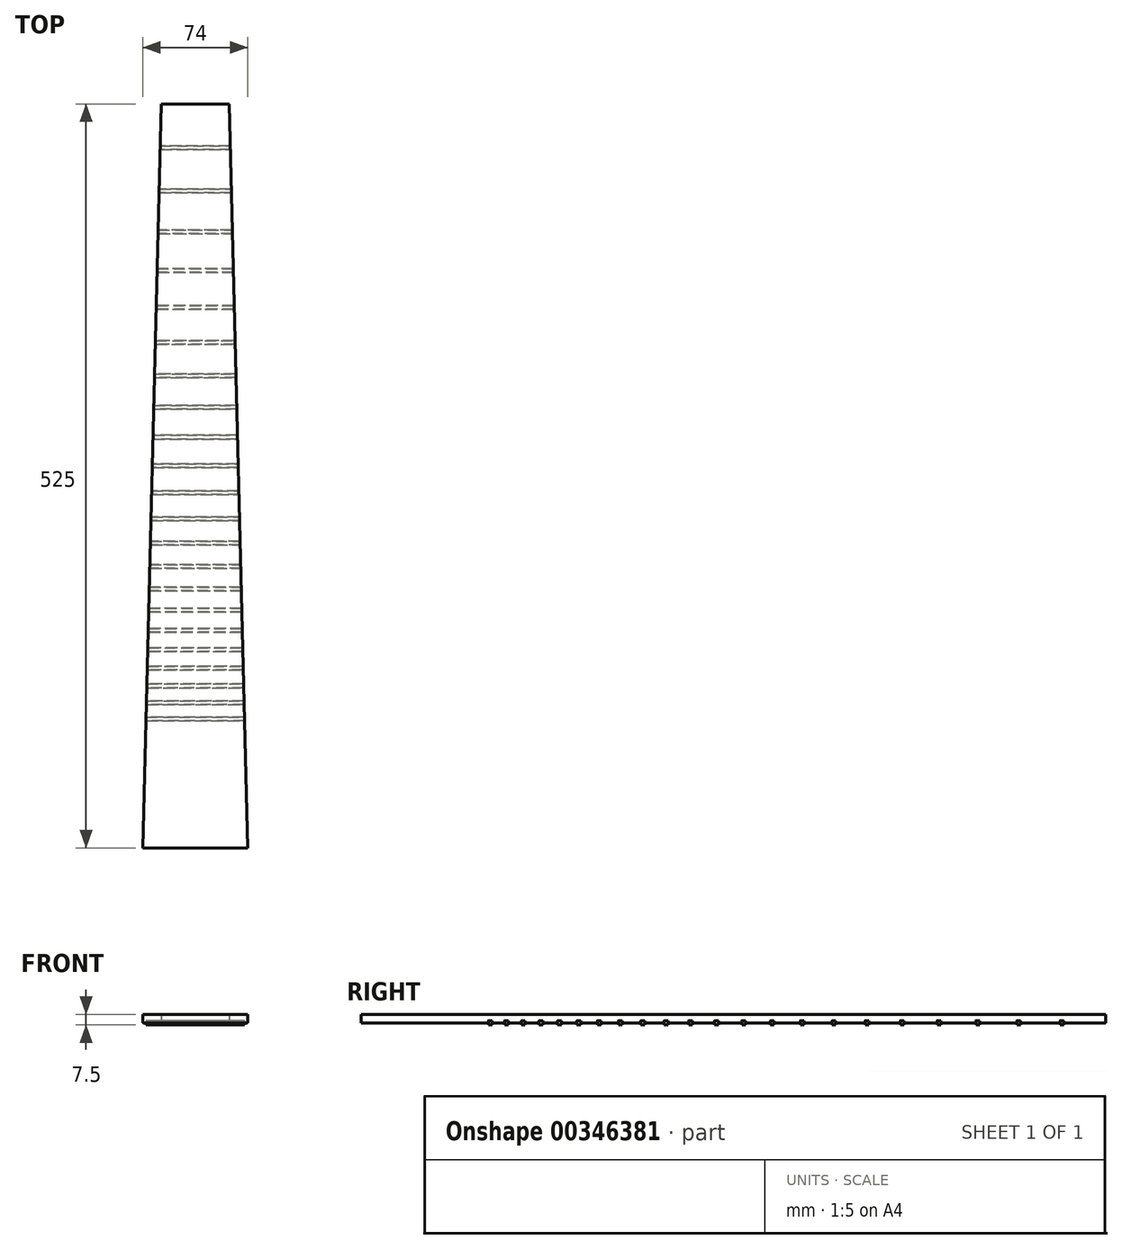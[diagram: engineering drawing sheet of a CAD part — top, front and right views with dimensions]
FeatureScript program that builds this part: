
annotation { "Feature Type Name" : "Feature", "Feature Type Description" : "" }
export const myFeature = defineFeature(function(context is Context, id is Id, definition is map)
    precondition{}
    {
        {
            var Q0;
            Q0=qCreatedBy(makeId("Top.planeOp"),FACE);
            var sketch = newSketch(context, id + "F0", { "sketchPlane" : qUnion([Q0])});
            skLineSegment(sketch, "E0", {"start": v(0, 0) * mm, "end": v(0, 525) * mm, "construction": true});
            skLineSegment(sketch, "E1", {"start": v(0, 525) * mm, "end": v(-24, 525) * mm});
            skLineSegment(sketch, "E2", {"start": v(0, 0) * mm, "end": v(-37, 0) * mm});
            skLineSegment(sketch, "E3", {"start": v(-37, 0) * mm, "end": v(-24, 525) * mm});
            skLineSegment(sketch, "E4", {"start": v(-24.73, 495.53) * mm, "end": v(0, 495.53) * mm});
            skLineSegment(sketch, "E5", {"start": v(-24.8, 492.92) * mm, "end": v(0, 492.92) * mm});
            skLineSegment(sketch, "E6", {"start": v(-25.48, 465.1) * mm, "end": v(0, 465.1) * mm});
            skLineSegment(sketch, "E7", {"start": v(-25.55, 462.49) * mm, "end": v(0, 462.49) * mm});
            skLineSegment(sketch, "E8", {"start": v(-26.2, 436.24) * mm, "end": v(0, 436.24) * mm});
            skLineSegment(sketch, "E9", {"start": v(-26.26, 433.62) * mm, "end": v(0, 433.62) * mm});
            skLineSegment(sketch, "E10", {"start": v(-26.88, 408.84) * mm, "end": v(0, 408.84) * mm});
            skLineSegment(sketch, "E11", {"start": v(-26.94, 406.23) * mm, "end": v(0, 406.23) * mm});
            skLineSegment(sketch, "E12", {"start": v(-27.52, 382.84) * mm, "end": v(0, 382.84) * mm});
            skLineSegment(sketch, "E13", {"start": v(-27.58, 380.22) * mm, "end": v(0, 380.22) * mm});
            skLineSegment(sketch, "E14", {"start": v(-28.13, 358.15) * mm, "end": v(0, 358.15) * mm});
            skLineSegment(sketch, "E15", {"start": v(-28.2, 355.53) * mm, "end": v(0, 355.53) * mm});
            skLineSegment(sketch, "E16", {"start": v(-28.71, 334.7) * mm, "end": v(0, 334.7) * mm});
            skLineSegment(sketch, "E17", {"start": v(-28.78, 332.08) * mm, "end": v(0, 332.08) * mm});
            skLineSegment(sketch, "E18", {"start": v(-29.26, 312.42) * mm, "end": v(0, 312.42) * mm});
            skLineSegment(sketch, "E19", {"start": v(-29.33, 309.8) * mm, "end": v(0, 309.8) * mm});
            skLineSegment(sketch, "E20", {"start": v(-29.79, 291.24) * mm, "end": v(0, 291.24) * mm});
            skLineSegment(sketch, "E21", {"start": v(-29.85, 288.62) * mm, "end": v(0, 288.62) * mm});
            skLineSegment(sketch, "E22", {"start": v(-30.29, 271.1) * mm, "end": v(0, 271.1) * mm});
            skLineSegment(sketch, "E23", {"start": v(-30.35, 268.48) * mm, "end": v(0, 268.48) * mm});
            skLineSegment(sketch, "E24", {"start": v(-30.76, 251.95) * mm, "end": v(0, 251.95) * mm});
            skLineSegment(sketch, "E25", {"start": v(-30.83, 249.33) * mm, "end": v(0, 249.33) * mm});
            skLineSegment(sketch, "E26", {"start": v(-31.21, 233.72) * mm, "end": v(0, 233.72) * mm});
            skLineSegment(sketch, "E27", {"start": v(-31.28, 231.1) * mm, "end": v(0, 231.1) * mm});
            skLineSegment(sketch, "E28", {"start": v(-31.64, 216.37) * mm, "end": v(0, 216.37) * mm});
            skLineSegment(sketch, "E29", {"start": v(-31.7, 213.76) * mm, "end": v(0, 213.76) * mm});
            skLineSegment(sketch, "E30", {"start": v(-32.05, 199.85) * mm, "end": v(0, 199.85) * mm});
            skLineSegment(sketch, "E31", {"start": v(-32.12, 197.23) * mm, "end": v(0, 197.23) * mm});
            skLineSegment(sketch, "E32", {"start": v(-32.44, 184.1) * mm, "end": v(0, 184.1) * mm});
            skLineSegment(sketch, "E33", {"start": v(-32.5, 181.5) * mm, "end": v(0, 181.5) * mm});
            skLineSegment(sketch, "E34", {"start": v(-32.81, 169.1) * mm, "end": v(0, 169.1) * mm});
            skLineSegment(sketch, "E35", {"start": v(-32.88, 166.49) * mm, "end": v(0, 166.49) * mm});
            skLineSegment(sketch, "E36", {"start": v(-33.17, 154.8) * mm, "end": v(0, 154.8) * mm});
            skLineSegment(sketch, "E37", {"start": v(-33.23, 152.18) * mm, "end": v(0, 152.18) * mm});
            skLineSegment(sketch, "E38", {"start": v(-33.5, 141.14) * mm, "end": v(0, 141.14) * mm});
            skLineSegment(sketch, "E39", {"start": v(-33.57, 138.53) * mm, "end": v(0, 138.53) * mm});
            skLineSegment(sketch, "E40", {"start": v(-33.83, 128.1) * mm, "end": v(0, 128.1) * mm});
            skLineSegment(sketch, "E41", {"start": v(-33.9, 125.5) * mm, "end": v(0, 125.5) * mm});
            skLineSegment(sketch, "E42", {"start": v(-34.14, 115.66) * mm, "end": v(0, 115.66) * mm});
            skLineSegment(sketch, "E43", {"start": v(-34.2, 113.04) * mm, "end": v(0, 113.04) * mm});
            skLineSegment(sketch, "E44", {"start": v(-34.43, 103.76) * mm, "end": v(0, 103.76) * mm});
            skLineSegment(sketch, "E45", {"start": v(-34.5, 101.14) * mm, "end": v(0, 101.14) * mm});
            skLineSegment(sketch, "E46", {"start": v(-34.71, 92.38) * mm, "end": v(0, 92.38) * mm});
            skLineSegment(sketch, "E47", {"start": v(-34.78, 89.77) * mm, "end": v(0, 89.77) * mm});
            skLineSegment(sketch, "E48.MirrorCS", {"start": v(0, 525) * mm, "end": v(24, 525) * mm});
            skLineSegment(sketch, "E49.MirrorCS", {"start": v(37, 0) * mm, "end": v(24, 525) * mm});
            skLineSegment(sketch, "E50.MirrorCS", {"start": v(24.73, 495.53) * mm, "end": v(0, 495.53) * mm});
            skLineSegment(sketch, "E51.MirrorCS", {"start": v(24.8, 492.92) * mm, "end": v(0, 492.92) * mm});
            skLineSegment(sketch, "E52.MirrorCS", {"start": v(25.48, 465.1) * mm, "end": v(0, 465.1) * mm});
            skLineSegment(sketch, "E53.MirrorCS", {"start": v(25.55, 462.49) * mm, "end": v(0, 462.49) * mm});
            skLineSegment(sketch, "E54.MirrorCS", {"start": v(26.2, 436.24) * mm, "end": v(0, 436.24) * mm});
            skLineSegment(sketch, "E55.MirrorCS", {"start": v(26.26, 433.62) * mm, "end": v(0, 433.62) * mm});
            skLineSegment(sketch, "E56.MirrorCS", {"start": v(26.88, 408.84) * mm, "end": v(0, 408.84) * mm});
            skLineSegment(sketch, "E57.MirrorCS", {"start": v(26.94, 406.23) * mm, "end": v(0, 406.23) * mm});
            skLineSegment(sketch, "E58.MirrorCS", {"start": v(27.52, 382.84) * mm, "end": v(0, 382.84) * mm});
            skLineSegment(sketch, "E59.MirrorCS", {"start": v(27.58, 380.22) * mm, "end": v(0, 380.22) * mm});
            skLineSegment(sketch, "E60.MirrorCS", {"start": v(28.13, 358.15) * mm, "end": v(0, 358.15) * mm});
            skLineSegment(sketch, "E61.MirrorCS", {"start": v(28.2, 355.53) * mm, "end": v(0, 355.53) * mm});
            skLineSegment(sketch, "E62.MirrorCS", {"start": v(28.71, 334.7) * mm, "end": v(0, 334.7) * mm});
            skLineSegment(sketch, "E63.MirrorCS", {"start": v(28.78, 332.08) * mm, "end": v(0, 332.08) * mm});
            skLineSegment(sketch, "E64.MirrorCS", {"start": v(29.26, 312.42) * mm, "end": v(0, 312.42) * mm});
            skLineSegment(sketch, "E65.MirrorCS", {"start": v(29.33, 309.8) * mm, "end": v(0, 309.8) * mm});
            skLineSegment(sketch, "E66.MirrorCS", {"start": v(29.79, 291.24) * mm, "end": v(0, 291.24) * mm});
            skLineSegment(sketch, "E67.MirrorCS", {"start": v(29.85, 288.62) * mm, "end": v(0, 288.62) * mm});
            skLineSegment(sketch, "E68.MirrorCS", {"start": v(30.29, 271.1) * mm, "end": v(0, 271.1) * mm});
            skLineSegment(sketch, "E69.MirrorCS", {"start": v(30.35, 268.48) * mm, "end": v(0, 268.48) * mm});
            skLineSegment(sketch, "E70.MirrorCS", {"start": v(30.76, 251.95) * mm, "end": v(0, 251.95) * mm});
            skLineSegment(sketch, "E71.MirrorCS", {"start": v(30.83, 249.33) * mm, "end": v(0, 249.33) * mm});
            skLineSegment(sketch, "E72.MirrorCS", {"start": v(31.21, 233.72) * mm, "end": v(0, 233.72) * mm});
            skLineSegment(sketch, "E73.MirrorCS", {"start": v(31.28, 231.1) * mm, "end": v(0, 231.1) * mm});
            skLineSegment(sketch, "E74.MirrorCS", {"start": v(31.64, 216.37) * mm, "end": v(0, 216.37) * mm});
            skLineSegment(sketch, "E75.MirrorCS", {"start": v(31.7, 213.76) * mm, "end": v(0, 213.76) * mm});
            skLineSegment(sketch, "E76.MirrorCS", {"start": v(32.05, 199.85) * mm, "end": v(0, 199.85) * mm});
            skLineSegment(sketch, "E77.MirrorCS", {"start": v(32.12, 197.23) * mm, "end": v(0, 197.23) * mm});
            skLineSegment(sketch, "E78.MirrorCS", {"start": v(32.44, 184.1) * mm, "end": v(0, 184.1) * mm});
            skLineSegment(sketch, "E79.MirrorCS", {"start": v(32.5, 181.5) * mm, "end": v(0, 181.5) * mm});
            skLineSegment(sketch, "E80.MirrorCS", {"start": v(32.81, 169.1) * mm, "end": v(0, 169.1) * mm});
            skLineSegment(sketch, "E81.MirrorCS", {"start": v(32.88, 166.49) * mm, "end": v(0, 166.49) * mm});
            skLineSegment(sketch, "E82.MirrorCS", {"start": v(33.17, 154.8) * mm, "end": v(0, 154.8) * mm});
            skLineSegment(sketch, "E83.MirrorCS", {"start": v(33.23, 152.18) * mm, "end": v(0, 152.18) * mm});
            skLineSegment(sketch, "E84.MirrorCS", {"start": v(33.5, 141.14) * mm, "end": v(0, 141.14) * mm});
            skLineSegment(sketch, "E85.MirrorCS", {"start": v(33.57, 138.53) * mm, "end": v(0, 138.53) * mm});
            skLineSegment(sketch, "E86.MirrorCS", {"start": v(33.83, 128.1) * mm, "end": v(0, 128.1) * mm});
            skLineSegment(sketch, "E87.MirrorCS", {"start": v(33.9, 125.5) * mm, "end": v(0, 125.5) * mm});
            skLineSegment(sketch, "E88.MirrorCS", {"start": v(34.14, 115.66) * mm, "end": v(0, 115.66) * mm});
            skLineSegment(sketch, "E89.MirrorCS", {"start": v(34.2, 113.04) * mm, "end": v(0, 113.04) * mm});
            skLineSegment(sketch, "E90.MirrorCS", {"start": v(34.43, 103.76) * mm, "end": v(0, 103.76) * mm});
            skLineSegment(sketch, "E91.MirrorCS", {"start": v(34.5, 101.14) * mm, "end": v(0, 101.14) * mm});
            skLineSegment(sketch, "E92.MirrorCS", {"start": v(0, 0) * mm, "end": v(37, 0) * mm});
            skLineSegment(sketch, "E93.MirrorCS", {"start": v(34.71, 92.38) * mm, "end": v(0, 92.38) * mm});
            skLineSegment(sketch, "E94.MirrorCS", {"start": v(34.78, 89.77) * mm, "end": v(0, 89.77) * mm});
            skSolve(sketch);
        }
        {
            var Q0;
            Q0=qSketchRegion(id+"F0",true);
            extrude(context, id + "F1", {"entities" : qUnion([Q0]), "depth" : 6 * mm});
        }
        {
            var Q0;
            {var subQ1=sQuery(id+"F0.wireOp",EDGE,"E4");Q0=makeQuery(id+"F0.imprint","IMPRINT",FACE,{"disambiguationData":[TD([[makeQuery(id+"F0.imprint","IMPRINT",EDGE,{"derivedFrom":subQ1}),-1.0]])]});}
            var Q1;
            {var subQ1=sQuery(id+"F0.wireOp",EDGE,"E6");Q1=makeQuery(id+"F0.imprint","IMPRINT",FACE,{"disambiguationData":[TD([[makeQuery(id+"F0.imprint","IMPRINT",EDGE,{"derivedFrom":subQ1}),-1.0]])]});}
            var Q2;
            {var subQ1=sQuery(id+"F0.wireOp",EDGE,"E8");Q2=makeQuery(id+"F0.imprint","IMPRINT",FACE,{"disambiguationData":[TD([[makeQuery(id+"F0.imprint","IMPRINT",EDGE,{"derivedFrom":subQ1}),-1.0]])]});}
            var Q3;
            {var subQ0=sQuery(id+"F0.wireOp",EDGE,"E10");Q3=makeQuery(id+"F0.imprint","IMPRINT",FACE,{"disambiguationData":[TD([[makeQuery(id+"F0.imprint","IMPRINT",EDGE,{"derivedFrom":subQ0}),-1.0]])]});}
            var Q4;
            {var subQ1=sQuery(id+"F0.wireOp",EDGE,"E12");Q4=makeQuery(id+"F0.imprint","IMPRINT",FACE,{"disambiguationData":[TD([[makeQuery(id+"F0.imprint","IMPRINT",EDGE,{"derivedFrom":subQ1}),-1.0]])]});}
            var Q5;
            {var subQ1=sQuery(id+"F0.wireOp",EDGE,"E14");Q5=makeQuery(id+"F0.imprint","IMPRINT",FACE,{"disambiguationData":[TD([[makeQuery(id+"F0.imprint","IMPRINT",EDGE,{"derivedFrom":subQ1}),-1.0]])]});}
            var Q6;
            {var subQ1=sQuery(id+"F0.wireOp",EDGE,"E16");Q6=makeQuery(id+"F0.imprint","IMPRINT",FACE,{"disambiguationData":[TD([[makeQuery(id+"F0.imprint","IMPRINT",EDGE,{"derivedFrom":subQ1}),-1.0]])]});}
            var Q7;
            {var subQ4=sQuery(id+"F0.wireOp",EDGE,"E18");Q7=makeQuery(id+"F0.imprint","IMPRINT",FACE,{"disambiguationData":[TD([[makeQuery(id+"F0.imprint","IMPRINT",EDGE,{"derivedFrom":subQ4}),-1.0]])]});}
            var Q8;
            {var subQ0=sQuery(id+"F0.wireOp",EDGE,"E20");Q8=makeQuery(id+"F0.imprint","IMPRINT",FACE,{"disambiguationData":[TD([[makeQuery(id+"F0.imprint","IMPRINT",EDGE,{"derivedFrom":subQ0}),-1.0]])]});}
            var Q9;
            {var subQ1=sQuery(id+"F0.wireOp",EDGE,"E22");Q9=makeQuery(id+"F0.imprint","IMPRINT",FACE,{"disambiguationData":[TD([[makeQuery(id+"F0.imprint","IMPRINT",EDGE,{"derivedFrom":subQ1}),-1.0]])]});}
            var Q10;
            {var subQ1=sQuery(id+"F0.wireOp",EDGE,"E24");Q10=makeQuery(id+"F0.imprint","IMPRINT",FACE,{"disambiguationData":[TD([[makeQuery(id+"F0.imprint","IMPRINT",EDGE,{"derivedFrom":subQ1}),-1.0]])]});}
            var Q11;
            {var subQ1=sQuery(id+"F0.wireOp",EDGE,"E26");Q11=makeQuery(id+"F0.imprint","IMPRINT",FACE,{"disambiguationData":[TD([[makeQuery(id+"F0.imprint","IMPRINT",EDGE,{"derivedFrom":subQ1}),-1.0]])]});}
            var Q12;
            {var subQ4=sQuery(id+"F0.wireOp",EDGE,"E28");Q12=makeQuery(id+"F0.imprint","IMPRINT",FACE,{"disambiguationData":[TD([[makeQuery(id+"F0.imprint","IMPRINT",EDGE,{"derivedFrom":subQ4}),-1.0]])]});}
            var Q13;
            {var subQ0=sQuery(id+"F0.wireOp",EDGE,"E30");Q13=makeQuery(id+"F0.imprint","IMPRINT",FACE,{"disambiguationData":[TD([[makeQuery(id+"F0.imprint","IMPRINT",EDGE,{"derivedFrom":subQ0}),-1.0]])]});}
            var Q14;
            {var subQ1=sQuery(id+"F0.wireOp",EDGE,"E32");Q14=makeQuery(id+"F0.imprint","IMPRINT",FACE,{"disambiguationData":[TD([[makeQuery(id+"F0.imprint","IMPRINT",EDGE,{"derivedFrom":subQ1}),-1.0]])]});}
            var Q15;
            {var subQ1=sQuery(id+"F0.wireOp",EDGE,"E34");Q15=makeQuery(id+"F0.imprint","IMPRINT",FACE,{"disambiguationData":[TD([[makeQuery(id+"F0.imprint","IMPRINT",EDGE,{"derivedFrom":subQ1}),-1.0]])]});}
            var Q16;
            {var subQ1=sQuery(id+"F0.wireOp",EDGE,"E36");Q16=makeQuery(id+"F0.imprint","IMPRINT",FACE,{"disambiguationData":[TD([[makeQuery(id+"F0.imprint","IMPRINT",EDGE,{"derivedFrom":subQ1}),-1.0]])]});}
            var Q17;
            {var subQ4=sQuery(id+"F0.wireOp",EDGE,"E38");Q17=makeQuery(id+"F0.imprint","IMPRINT",FACE,{"disambiguationData":[TD([[makeQuery(id+"F0.imprint","IMPRINT",EDGE,{"derivedFrom":subQ4}),-1.0]])]});}
            var Q18;
            {var subQ0=sQuery(id+"F0.wireOp",EDGE,"E40");Q18=makeQuery(id+"F0.imprint","IMPRINT",FACE,{"disambiguationData":[TD([[makeQuery(id+"F0.imprint","IMPRINT",EDGE,{"derivedFrom":subQ0}),-1.0]])]});}
            var Q19;
            {var subQ1=sQuery(id+"F0.wireOp",EDGE,"E46");Q19=makeQuery(id+"F0.imprint","IMPRINT",FACE,{"disambiguationData":[TD([[makeQuery(id+"F0.imprint","IMPRINT",EDGE,{"derivedFrom":subQ1}),-1.0]])]});}
            var Q20;
            {var subQ1=sQuery(id+"F0.wireOp",EDGE,"E44");Q20=makeQuery(id+"F0.imprint","IMPRINT",FACE,{"disambiguationData":[TD([[makeQuery(id+"F0.imprint","IMPRINT",EDGE,{"derivedFrom":subQ1}),-1.0]])]});}
            var Q21;
            {var subQ4=sQuery(id+"F0.wireOp",EDGE,"E42");Q21=makeQuery(id+"F0.imprint","IMPRINT",FACE,{"disambiguationData":[TD([[makeQuery(id+"F0.imprint","IMPRINT",EDGE,{"derivedFrom":subQ4}),-1.0]])]});}
            extrude(context, id + "F2", {"entities" : qUnion([Q0, Q1, Q2, Q3, Q4, Q5, Q6, Q7, Q8, Q9, Q10, Q11, Q12, Q13, Q14, Q15, Q16, Q17, Q18, Q19, Q20, Q21]), "endBound" : BoundingType.SYMMETRIC, "depth" : 3 * mm});
        }
        {
            var Q0;
            Q0=makeQuery(id+"F1.opExtrude","CAP_EDGE",EDGE,{"disambiguationData":[OSD([sQuery(id+"F0.wireOp",EDGE,"E3")])],"isStart":true});
            var Q1;
            Q1=makeQuery(id+"F1.opExtrude","CAP_EDGE",EDGE,{"disambiguationData":[OSD([sQuery(id+"F0.wireOp",EDGE,"E49.MirrorCS")])],"isStart":true});
            fillet(context, id + "F3", {"entities" : qUnion([Q0, Q1]), "radius" : 0.5 * mm, "tangentPropagation" : true, "allowEdgeOverflow" : false});
        }
        {
            var Q0;
            Q0=makeQuery(id+"F2.opExtrude","SWEPT_BODY",BODY,{"disambiguationData":[OSD([sQuery(id+"F0.wireOp",EDGE,"E3"),sQuery(id+"F0.wireOp",EDGE,"E46"),sQuery(id+"F0.wireOp",EDGE,"E47"),sQuery(id+"F0.wireOp",EDGE,"E49.MirrorCS"),sQuery(id+"F0.wireOp",EDGE,"E93.MirrorCS"),sQuery(id+"F0.wireOp",EDGE,"E94.MirrorCS")])]});
            var Q1;
            Q1=makeQuery(id+"F2.opExtrude","SWEPT_BODY",BODY,{"disambiguationData":[OSD([sQuery(id+"F0.wireOp",EDGE,"E3"),sQuery(id+"F0.wireOp",EDGE,"E44"),sQuery(id+"F0.wireOp",EDGE,"E45"),sQuery(id+"F0.wireOp",EDGE,"E49.MirrorCS"),sQuery(id+"F0.wireOp",EDGE,"E90.MirrorCS"),sQuery(id+"F0.wireOp",EDGE,"E91.MirrorCS")])]});
            var Q2;
            Q2=makeQuery(id+"F2.opExtrude","SWEPT_BODY",BODY,{"disambiguationData":[OSD([sQuery(id+"F0.wireOp",EDGE,"E3"),sQuery(id+"F0.wireOp",EDGE,"E42"),sQuery(id+"F0.wireOp",EDGE,"E43"),sQuery(id+"F0.wireOp",EDGE,"E49.MirrorCS"),sQuery(id+"F0.wireOp",EDGE,"E88.MirrorCS"),sQuery(id+"F0.wireOp",EDGE,"E89.MirrorCS")])]});
            var Q3;
            Q3=makeQuery(id+"F2.opExtrude","SWEPT_BODY",BODY,{"disambiguationData":[OSD([sQuery(id+"F0.wireOp",EDGE,"E3"),sQuery(id+"F0.wireOp",EDGE,"E40"),sQuery(id+"F0.wireOp",EDGE,"E41"),sQuery(id+"F0.wireOp",EDGE,"E49.MirrorCS"),sQuery(id+"F0.wireOp",EDGE,"E86.MirrorCS"),sQuery(id+"F0.wireOp",EDGE,"E87.MirrorCS")])]});
            var Q4;
            Q4=makeQuery(id+"F2.opExtrude","SWEPT_BODY",BODY,{"disambiguationData":[OSD([sQuery(id+"F0.wireOp",EDGE,"E3"),sQuery(id+"F0.wireOp",EDGE,"E38"),sQuery(id+"F0.wireOp",EDGE,"E39"),sQuery(id+"F0.wireOp",EDGE,"E49.MirrorCS"),sQuery(id+"F0.wireOp",EDGE,"E84.MirrorCS"),sQuery(id+"F0.wireOp",EDGE,"E85.MirrorCS")])]});
            var Q5;
            Q5=makeQuery(id+"F2.opExtrude","SWEPT_BODY",BODY,{"disambiguationData":[OSD([sQuery(id+"F0.wireOp",EDGE,"E3"),sQuery(id+"F0.wireOp",EDGE,"E36"),sQuery(id+"F0.wireOp",EDGE,"E37"),sQuery(id+"F0.wireOp",EDGE,"E49.MirrorCS"),sQuery(id+"F0.wireOp",EDGE,"E82.MirrorCS"),sQuery(id+"F0.wireOp",EDGE,"E83.MirrorCS")])]});
            var Q6;
            Q6=makeQuery(id+"F2.opExtrude","SWEPT_BODY",BODY,{"disambiguationData":[OSD([sQuery(id+"F0.wireOp",EDGE,"E3"),sQuery(id+"F0.wireOp",EDGE,"E34"),sQuery(id+"F0.wireOp",EDGE,"E35"),sQuery(id+"F0.wireOp",EDGE,"E49.MirrorCS"),sQuery(id+"F0.wireOp",EDGE,"E80.MirrorCS"),sQuery(id+"F0.wireOp",EDGE,"E81.MirrorCS")])]});
            var Q7;
            Q7=makeQuery(id+"F2.opExtrude","SWEPT_BODY",BODY,{"disambiguationData":[OSD([sQuery(id+"F0.wireOp",EDGE,"E3"),sQuery(id+"F0.wireOp",EDGE,"E32"),sQuery(id+"F0.wireOp",EDGE,"E33"),sQuery(id+"F0.wireOp",EDGE,"E49.MirrorCS"),sQuery(id+"F0.wireOp",EDGE,"E78.MirrorCS"),sQuery(id+"F0.wireOp",EDGE,"E79.MirrorCS")])]});
            var Q8;
            Q8=makeQuery(id+"F2.opExtrude","SWEPT_BODY",BODY,{"disambiguationData":[OSD([sQuery(id+"F0.wireOp",EDGE,"E3"),sQuery(id+"F0.wireOp",EDGE,"E30"),sQuery(id+"F0.wireOp",EDGE,"E31"),sQuery(id+"F0.wireOp",EDGE,"E49.MirrorCS"),sQuery(id+"F0.wireOp",EDGE,"E76.MirrorCS"),sQuery(id+"F0.wireOp",EDGE,"E77.MirrorCS")])]});
            var Q9;
            Q9=makeQuery(id+"F2.opExtrude","SWEPT_BODY",BODY,{"disambiguationData":[OSD([sQuery(id+"F0.wireOp",EDGE,"E3"),sQuery(id+"F0.wireOp",EDGE,"E28"),sQuery(id+"F0.wireOp",EDGE,"E29"),sQuery(id+"F0.wireOp",EDGE,"E49.MirrorCS"),sQuery(id+"F0.wireOp",EDGE,"E74.MirrorCS"),sQuery(id+"F0.wireOp",EDGE,"E75.MirrorCS")])]});
            var Q10;
            Q10=makeQuery(id+"F2.opExtrude","SWEPT_BODY",BODY,{"disambiguationData":[OSD([sQuery(id+"F0.wireOp",EDGE,"E3"),sQuery(id+"F0.wireOp",EDGE,"E26"),sQuery(id+"F0.wireOp",EDGE,"E27"),sQuery(id+"F0.wireOp",EDGE,"E49.MirrorCS"),sQuery(id+"F0.wireOp",EDGE,"E72.MirrorCS"),sQuery(id+"F0.wireOp",EDGE,"E73.MirrorCS")])]});
            var Q11;
            Q11=makeQuery(id+"F2.opExtrude","SWEPT_BODY",BODY,{"disambiguationData":[OSD([sQuery(id+"F0.wireOp",EDGE,"E3"),sQuery(id+"F0.wireOp",EDGE,"E24"),sQuery(id+"F0.wireOp",EDGE,"E25"),sQuery(id+"F0.wireOp",EDGE,"E49.MirrorCS"),sQuery(id+"F0.wireOp",EDGE,"E70.MirrorCS"),sQuery(id+"F0.wireOp",EDGE,"E71.MirrorCS")])]});
            var Q12;
            Q12=makeQuery(id+"F2.opExtrude","SWEPT_BODY",BODY,{"disambiguationData":[OSD([sQuery(id+"F0.wireOp",EDGE,"E3"),sQuery(id+"F0.wireOp",EDGE,"E22"),sQuery(id+"F0.wireOp",EDGE,"E23"),sQuery(id+"F0.wireOp",EDGE,"E49.MirrorCS"),sQuery(id+"F0.wireOp",EDGE,"E68.MirrorCS"),sQuery(id+"F0.wireOp",EDGE,"E69.MirrorCS")])]});
            var Q13;
            Q13=makeQuery(id+"F2.opExtrude","SWEPT_BODY",BODY,{"disambiguationData":[OSD([sQuery(id+"F0.wireOp",EDGE,"E3"),sQuery(id+"F0.wireOp",EDGE,"E20"),sQuery(id+"F0.wireOp",EDGE,"E21"),sQuery(id+"F0.wireOp",EDGE,"E49.MirrorCS"),sQuery(id+"F0.wireOp",EDGE,"E66.MirrorCS"),sQuery(id+"F0.wireOp",EDGE,"E67.MirrorCS")])]});
            var Q14;
            Q14=makeQuery(id+"F2.opExtrude","SWEPT_BODY",BODY,{"disambiguationData":[OSD([sQuery(id+"F0.wireOp",EDGE,"E3"),sQuery(id+"F0.wireOp",EDGE,"E18"),sQuery(id+"F0.wireOp",EDGE,"E19"),sQuery(id+"F0.wireOp",EDGE,"E49.MirrorCS"),sQuery(id+"F0.wireOp",EDGE,"E64.MirrorCS"),sQuery(id+"F0.wireOp",EDGE,"E65.MirrorCS")])]});
            var Q15;
            Q15=makeQuery(id+"F2.opExtrude","SWEPT_BODY",BODY,{"disambiguationData":[OSD([sQuery(id+"F0.wireOp",EDGE,"E3"),sQuery(id+"F0.wireOp",EDGE,"E16"),sQuery(id+"F0.wireOp",EDGE,"E17"),sQuery(id+"F0.wireOp",EDGE,"E49.MirrorCS"),sQuery(id+"F0.wireOp",EDGE,"E62.MirrorCS"),sQuery(id+"F0.wireOp",EDGE,"E63.MirrorCS")])]});
            var Q16;
            Q16=makeQuery(id+"F2.opExtrude","SWEPT_BODY",BODY,{"disambiguationData":[OSD([sQuery(id+"F0.wireOp",EDGE,"E3"),sQuery(id+"F0.wireOp",EDGE,"E14"),sQuery(id+"F0.wireOp",EDGE,"E15"),sQuery(id+"F0.wireOp",EDGE,"E49.MirrorCS"),sQuery(id+"F0.wireOp",EDGE,"E60.MirrorCS"),sQuery(id+"F0.wireOp",EDGE,"E61.MirrorCS")])]});
            var Q17;
            Q17=makeQuery(id+"F2.opExtrude","SWEPT_BODY",BODY,{"disambiguationData":[OSD([sQuery(id+"F0.wireOp",EDGE,"E3"),sQuery(id+"F0.wireOp",EDGE,"E12"),sQuery(id+"F0.wireOp",EDGE,"E13"),sQuery(id+"F0.wireOp",EDGE,"E49.MirrorCS"),sQuery(id+"F0.wireOp",EDGE,"E58.MirrorCS"),sQuery(id+"F0.wireOp",EDGE,"E59.MirrorCS")])]});
            var Q18;
            Q18=makeQuery(id+"F2.opExtrude","SWEPT_BODY",BODY,{"disambiguationData":[OSD([sQuery(id+"F0.wireOp",EDGE,"E3"),sQuery(id+"F0.wireOp",EDGE,"E10"),sQuery(id+"F0.wireOp",EDGE,"E11"),sQuery(id+"F0.wireOp",EDGE,"E49.MirrorCS"),sQuery(id+"F0.wireOp",EDGE,"E56.MirrorCS"),sQuery(id+"F0.wireOp",EDGE,"E57.MirrorCS")])]});
            var Q19;
            Q19=makeQuery(id+"F2.opExtrude","SWEPT_BODY",BODY,{"disambiguationData":[OSD([sQuery(id+"F0.wireOp",EDGE,"E3"),sQuery(id+"F0.wireOp",EDGE,"E8"),sQuery(id+"F0.wireOp",EDGE,"E9"),sQuery(id+"F0.wireOp",EDGE,"E49.MirrorCS"),sQuery(id+"F0.wireOp",EDGE,"E54.MirrorCS"),sQuery(id+"F0.wireOp",EDGE,"E55.MirrorCS")])]});
            var Q20;
            Q20=makeQuery(id+"F2.opExtrude","SWEPT_BODY",BODY,{"disambiguationData":[OSD([sQuery(id+"F0.wireOp",EDGE,"E3"),sQuery(id+"F0.wireOp",EDGE,"E6"),sQuery(id+"F0.wireOp",EDGE,"E7"),sQuery(id+"F0.wireOp",EDGE,"E49.MirrorCS"),sQuery(id+"F0.wireOp",EDGE,"E52.MirrorCS"),sQuery(id+"F0.wireOp",EDGE,"E53.MirrorCS")])]});
            var Q21;
            Q21=makeQuery(id+"F2.opExtrude","SWEPT_BODY",BODY,{"disambiguationData":[OSD([sQuery(id+"F0.wireOp",EDGE,"E3"),sQuery(id+"F0.wireOp",EDGE,"E4"),sQuery(id+"F0.wireOp",EDGE,"E5"),sQuery(id+"F0.wireOp",EDGE,"E49.MirrorCS"),sQuery(id+"F0.wireOp",EDGE,"E50.MirrorCS"),sQuery(id+"F0.wireOp",EDGE,"E51.MirrorCS")])]});
            var Q22;
            Q22=makeQuery(id+"F1.opExtrude","SWEPT_BODY",BODY,{"disambiguationData":[OSD([sQuery(id+"F0.wireOp",EDGE,"E1"),sQuery(id+"F0.wireOp",EDGE,"E2"),sQuery(id+"F0.wireOp",EDGE,"E3"),sQuery(id+"F0.wireOp",EDGE,"E48.MirrorCS"),sQuery(id+"F0.wireOp",EDGE,"E49.MirrorCS"),sQuery(id+"F0.wireOp",EDGE,"E92.MirrorCS")])]});
            booleanBodies(context, id + "F4", {"operationType" : BooleanOperationType.SUBTRACTION, "tools" : qUnion([Q0, Q1, Q2, Q3, Q4, Q5, Q6, Q7, Q8, Q9, Q10, Q11, Q12, Q13, Q14, Q15, Q16, Q17, Q18, Q19, Q20, Q21]), "targets" : qUnion([Q22]), "keepTools" : true});
        }
        {
            var Q0;
            {var subQ0=sQuery(id+"F0.wireOp",EDGE,"E3");Q0=makeQuery(id+"F2.opExtrude","CAP_EDGE",EDGE,{"disambiguationData":[OSD([subQ0]),TDD([makeQuery(id+"F0.imprint","IMPRINT",EDGE,{"disambiguationData":[TD([[makeQuery(id+"F0.imprint","INTERSECT",VERTEX,{"derivedFrom":[subQ0,sQuery(id+"F0.wireOp",EDGE,"E4")]}),1.0]])],"derivedFrom":subQ0})])],"isStart":false});}
            var Q1;
            {var subQ0=sQuery(id+"F0.wireOp",EDGE,"E49.MirrorCS");Q1=makeQuery(id+"F2.opExtrude","CAP_EDGE",EDGE,{"disambiguationData":[OSD([subQ0]),TDD([makeQuery(id+"F0.imprint","IMPRINT",EDGE,{"disambiguationData":[TD([[makeQuery(id+"F0.imprint","INTERSECT",VERTEX,{"derivedFrom":[subQ0,sQuery(id+"F0.wireOp",EDGE,"E50.MirrorCS")]}),1.0]])],"derivedFrom":subQ0})])],"isStart":false});}
            var Q2;
            {var subQ0=sQuery(id+"F0.wireOp",EDGE,"E49.MirrorCS");Q2=makeQuery(id+"F2.opExtrude","CAP_EDGE",EDGE,{"disambiguationData":[OSD([subQ0]),TDD([makeQuery(id+"F0.imprint","IMPRINT",EDGE,{"disambiguationData":[TD([[makeQuery(id+"F0.imprint","INTERSECT",VERTEX,{"derivedFrom":[subQ0,sQuery(id+"F0.wireOp",EDGE,"E52.MirrorCS")]}),1.0]])],"derivedFrom":subQ0})])],"isStart":false});}
            var Q3;
            {var subQ0=sQuery(id+"F0.wireOp",EDGE,"E3");Q3=makeQuery(id+"F2.opExtrude","CAP_EDGE",EDGE,{"disambiguationData":[OSD([subQ0]),TDD([makeQuery(id+"F0.imprint","IMPRINT",EDGE,{"disambiguationData":[TD([[makeQuery(id+"F0.imprint","INTERSECT",VERTEX,{"derivedFrom":[subQ0,sQuery(id+"F0.wireOp",EDGE,"E6")]}),1.0]])],"derivedFrom":subQ0})])],"isStart":false});}
            var Q4;
            {var subQ0=sQuery(id+"F0.wireOp",EDGE,"E3");Q4=makeQuery(id+"F2.opExtrude","CAP_EDGE",EDGE,{"disambiguationData":[OSD([subQ0]),TDD([makeQuery(id+"F0.imprint","IMPRINT",EDGE,{"disambiguationData":[TD([[makeQuery(id+"F0.imprint","INTERSECT",VERTEX,{"derivedFrom":[subQ0,sQuery(id+"F0.wireOp",EDGE,"E8")]}),1.0]])],"derivedFrom":subQ0})])],"isStart":false});}
            var Q5;
            {var subQ0=sQuery(id+"F0.wireOp",EDGE,"E49.MirrorCS");Q5=makeQuery(id+"F2.opExtrude","CAP_EDGE",EDGE,{"disambiguationData":[OSD([subQ0]),TDD([makeQuery(id+"F0.imprint","IMPRINT",EDGE,{"disambiguationData":[TD([[makeQuery(id+"F0.imprint","INTERSECT",VERTEX,{"derivedFrom":[subQ0,sQuery(id+"F0.wireOp",EDGE,"E54.MirrorCS")]}),1.0]])],"derivedFrom":subQ0})])],"isStart":false});}
            var Q6;
            {var subQ0=sQuery(id+"F0.wireOp",EDGE,"E3");Q6=makeQuery(id+"F2.opExtrude","CAP_EDGE",EDGE,{"disambiguationData":[OSD([subQ0]),TDD([makeQuery(id+"F0.imprint","IMPRINT",EDGE,{"disambiguationData":[TD([[makeQuery(id+"F0.imprint","INTERSECT",VERTEX,{"derivedFrom":[subQ0,sQuery(id+"F0.wireOp",EDGE,"E10")]}),1.0]])],"derivedFrom":subQ0})])],"isStart":false});}
            var Q7;
            {var subQ0=sQuery(id+"F0.wireOp",EDGE,"E49.MirrorCS");Q7=makeQuery(id+"F2.opExtrude","CAP_EDGE",EDGE,{"disambiguationData":[OSD([subQ0]),TDD([makeQuery(id+"F0.imprint","IMPRINT",EDGE,{"disambiguationData":[TD([[makeQuery(id+"F0.imprint","INTERSECT",VERTEX,{"derivedFrom":[subQ0,sQuery(id+"F0.wireOp",EDGE,"E56.MirrorCS")]}),1.0]])],"derivedFrom":subQ0})])],"isStart":false});}
            var Q8;
            {var subQ0=sQuery(id+"F0.wireOp",EDGE,"E49.MirrorCS");Q8=makeQuery(id+"F2.opExtrude","CAP_EDGE",EDGE,{"disambiguationData":[OSD([subQ0]),TDD([makeQuery(id+"F0.imprint","IMPRINT",EDGE,{"disambiguationData":[TD([[makeQuery(id+"F0.imprint","INTERSECT",VERTEX,{"derivedFrom":[subQ0,sQuery(id+"F0.wireOp",EDGE,"E58.MirrorCS")]}),1.0]])],"derivedFrom":subQ0})])],"isStart":false});}
            var Q9;
            {var subQ0=sQuery(id+"F0.wireOp",EDGE,"E3");Q9=makeQuery(id+"F2.opExtrude","CAP_EDGE",EDGE,{"disambiguationData":[OSD([subQ0]),TDD([makeQuery(id+"F0.imprint","IMPRINT",EDGE,{"disambiguationData":[TD([[makeQuery(id+"F0.imprint","INTERSECT",VERTEX,{"derivedFrom":[subQ0,sQuery(id+"F0.wireOp",EDGE,"E12")]}),1.0]])],"derivedFrom":subQ0})])],"isStart":false});}
            var Q10;
            {var subQ0=sQuery(id+"F0.wireOp",EDGE,"E3");Q10=makeQuery(id+"F2.opExtrude","CAP_EDGE",EDGE,{"disambiguationData":[OSD([subQ0]),TDD([makeQuery(id+"F0.imprint","IMPRINT",EDGE,{"disambiguationData":[TD([[makeQuery(id+"F0.imprint","INTERSECT",VERTEX,{"derivedFrom":[subQ0,sQuery(id+"F0.wireOp",EDGE,"E14")]}),1.0]])],"derivedFrom":subQ0})])],"isStart":false});}
            var Q11;
            {var subQ0=sQuery(id+"F0.wireOp",EDGE,"E49.MirrorCS");Q11=makeQuery(id+"F2.opExtrude","CAP_EDGE",EDGE,{"disambiguationData":[OSD([subQ0]),TDD([makeQuery(id+"F0.imprint","IMPRINT",EDGE,{"disambiguationData":[TD([[makeQuery(id+"F0.imprint","INTERSECT",VERTEX,{"derivedFrom":[subQ0,sQuery(id+"F0.wireOp",EDGE,"E60.MirrorCS")]}),1.0]])],"derivedFrom":subQ0})])],"isStart":false});}
            var Q12;
            {var subQ0=sQuery(id+"F0.wireOp",EDGE,"E49.MirrorCS");Q12=makeQuery(id+"F2.opExtrude","CAP_EDGE",EDGE,{"disambiguationData":[OSD([subQ0]),TDD([makeQuery(id+"F0.imprint","IMPRINT",EDGE,{"disambiguationData":[TD([[makeQuery(id+"F0.imprint","INTERSECT",VERTEX,{"derivedFrom":[subQ0,sQuery(id+"F0.wireOp",EDGE,"E62.MirrorCS")]}),1.0]])],"derivedFrom":subQ0})])],"isStart":false});}
            var Q13;
            {var subQ0=sQuery(id+"F0.wireOp",EDGE,"E3");Q13=makeQuery(id+"F2.opExtrude","CAP_EDGE",EDGE,{"disambiguationData":[OSD([subQ0]),TDD([makeQuery(id+"F0.imprint","IMPRINT",EDGE,{"disambiguationData":[TD([[makeQuery(id+"F0.imprint","INTERSECT",VERTEX,{"derivedFrom":[subQ0,sQuery(id+"F0.wireOp",EDGE,"E16")]}),1.0]])],"derivedFrom":subQ0})])],"isStart":false});}
            var Q14;
            {var subQ0=sQuery(id+"F0.wireOp",EDGE,"E3");Q14=makeQuery(id+"F2.opExtrude","CAP_EDGE",EDGE,{"disambiguationData":[OSD([subQ0]),TDD([makeQuery(id+"F0.imprint","IMPRINT",EDGE,{"disambiguationData":[TD([[makeQuery(id+"F0.imprint","INTERSECT",VERTEX,{"derivedFrom":[subQ0,sQuery(id+"F0.wireOp",EDGE,"E18")]}),1.0]])],"derivedFrom":subQ0})])],"isStart":false});}
            var Q15;
            {var subQ0=sQuery(id+"F0.wireOp",EDGE,"E49.MirrorCS");Q15=makeQuery(id+"F2.opExtrude","CAP_EDGE",EDGE,{"disambiguationData":[OSD([subQ0]),TDD([makeQuery(id+"F0.imprint","IMPRINT",EDGE,{"disambiguationData":[TD([[makeQuery(id+"F0.imprint","INTERSECT",VERTEX,{"derivedFrom":[subQ0,sQuery(id+"F0.wireOp",EDGE,"E64.MirrorCS")]}),1.0]])],"derivedFrom":subQ0})])],"isStart":false});}
            var Q16;
            {var subQ0=sQuery(id+"F0.wireOp",EDGE,"E49.MirrorCS");Q16=makeQuery(id+"F2.opExtrude","CAP_EDGE",EDGE,{"disambiguationData":[OSD([subQ0]),TDD([makeQuery(id+"F0.imprint","IMPRINT",EDGE,{"disambiguationData":[TD([[makeQuery(id+"F0.imprint","INTERSECT",VERTEX,{"derivedFrom":[subQ0,sQuery(id+"F0.wireOp",EDGE,"E66.MirrorCS")]}),1.0]])],"derivedFrom":subQ0})])],"isStart":false});}
            var Q17;
            {var subQ0=sQuery(id+"F0.wireOp",EDGE,"E3");Q17=makeQuery(id+"F2.opExtrude","CAP_EDGE",EDGE,{"disambiguationData":[OSD([subQ0]),TDD([makeQuery(id+"F0.imprint","IMPRINT",EDGE,{"disambiguationData":[TD([[makeQuery(id+"F0.imprint","INTERSECT",VERTEX,{"derivedFrom":[subQ0,sQuery(id+"F0.wireOp",EDGE,"E20")]}),1.0]])],"derivedFrom":subQ0})])],"isStart":false});}
            var Q18;
            {var subQ0=sQuery(id+"F0.wireOp",EDGE,"E3");Q18=makeQuery(id+"F2.opExtrude","CAP_EDGE",EDGE,{"disambiguationData":[OSD([subQ0]),TDD([makeQuery(id+"F0.imprint","IMPRINT",EDGE,{"disambiguationData":[TD([[makeQuery(id+"F0.imprint","INTERSECT",VERTEX,{"derivedFrom":[subQ0,sQuery(id+"F0.wireOp",EDGE,"E22")]}),1.0]])],"derivedFrom":subQ0})])],"isStart":false});}
            var Q19;
            {var subQ0=sQuery(id+"F0.wireOp",EDGE,"E49.MirrorCS");Q19=makeQuery(id+"F2.opExtrude","CAP_EDGE",EDGE,{"disambiguationData":[OSD([subQ0]),TDD([makeQuery(id+"F0.imprint","IMPRINT",EDGE,{"disambiguationData":[TD([[makeQuery(id+"F0.imprint","INTERSECT",VERTEX,{"derivedFrom":[subQ0,sQuery(id+"F0.wireOp",EDGE,"E68.MirrorCS")]}),1.0]])],"derivedFrom":subQ0})])],"isStart":false});}
            var Q20;
            {var subQ0=sQuery(id+"F0.wireOp",EDGE,"E49.MirrorCS");Q20=makeQuery(id+"F2.opExtrude","CAP_EDGE",EDGE,{"disambiguationData":[OSD([subQ0]),TDD([makeQuery(id+"F0.imprint","IMPRINT",EDGE,{"disambiguationData":[TD([[makeQuery(id+"F0.imprint","INTERSECT",VERTEX,{"derivedFrom":[subQ0,sQuery(id+"F0.wireOp",EDGE,"E70.MirrorCS")]}),1.0]])],"derivedFrom":subQ0})])],"isStart":false});}
            var Q21;
            {var subQ0=sQuery(id+"F0.wireOp",EDGE,"E3");Q21=makeQuery(id+"F2.opExtrude","CAP_EDGE",EDGE,{"disambiguationData":[OSD([subQ0]),TDD([makeQuery(id+"F0.imprint","IMPRINT",EDGE,{"disambiguationData":[TD([[makeQuery(id+"F0.imprint","INTERSECT",VERTEX,{"derivedFrom":[subQ0,sQuery(id+"F0.wireOp",EDGE,"E24")]}),1.0]])],"derivedFrom":subQ0})])],"isStart":false});}
            var Q22;
            {var subQ0=sQuery(id+"F0.wireOp",EDGE,"E3");Q22=makeQuery(id+"F2.opExtrude","CAP_EDGE",EDGE,{"disambiguationData":[OSD([subQ0]),TDD([makeQuery(id+"F0.imprint","IMPRINT",EDGE,{"disambiguationData":[TD([[makeQuery(id+"F0.imprint","INTERSECT",VERTEX,{"derivedFrom":[subQ0,sQuery(id+"F0.wireOp",EDGE,"E26")]}),1.0]])],"derivedFrom":subQ0})])],"isStart":false});}
            var Q23;
            {var subQ0=sQuery(id+"F0.wireOp",EDGE,"E49.MirrorCS");Q23=makeQuery(id+"F2.opExtrude","CAP_EDGE",EDGE,{"disambiguationData":[OSD([subQ0]),TDD([makeQuery(id+"F0.imprint","IMPRINT",EDGE,{"disambiguationData":[TD([[makeQuery(id+"F0.imprint","INTERSECT",VERTEX,{"derivedFrom":[subQ0,sQuery(id+"F0.wireOp",EDGE,"E72.MirrorCS")]}),1.0]])],"derivedFrom":subQ0})])],"isStart":false});}
            var Q24;
            {var subQ0=sQuery(id+"F0.wireOp",EDGE,"E3");Q24=makeQuery(id+"F2.opExtrude","CAP_EDGE",EDGE,{"disambiguationData":[OSD([subQ0]),TDD([makeQuery(id+"F0.imprint","IMPRINT",EDGE,{"disambiguationData":[TD([[makeQuery(id+"F0.imprint","INTERSECT",VERTEX,{"derivedFrom":[subQ0,sQuery(id+"F0.wireOp",EDGE,"E28")]}),1.0]])],"derivedFrom":subQ0})])],"isStart":false});}
            var Q25;
            {var subQ0=sQuery(id+"F0.wireOp",EDGE,"E49.MirrorCS");Q25=makeQuery(id+"F2.opExtrude","CAP_EDGE",EDGE,{"disambiguationData":[OSD([subQ0]),TDD([makeQuery(id+"F0.imprint","IMPRINT",EDGE,{"disambiguationData":[TD([[makeQuery(id+"F0.imprint","INTERSECT",VERTEX,{"derivedFrom":[subQ0,sQuery(id+"F0.wireOp",EDGE,"E74.MirrorCS")]}),1.0]])],"derivedFrom":subQ0})])],"isStart":false});}
            var Q26;
            {var subQ0=sQuery(id+"F0.wireOp",EDGE,"E49.MirrorCS");Q26=makeQuery(id+"F2.opExtrude","CAP_EDGE",EDGE,{"disambiguationData":[OSD([subQ0]),TDD([makeQuery(id+"F0.imprint","IMPRINT",EDGE,{"disambiguationData":[TD([[makeQuery(id+"F0.imprint","INTERSECT",VERTEX,{"derivedFrom":[subQ0,sQuery(id+"F0.wireOp",EDGE,"E76.MirrorCS")]}),1.0]])],"derivedFrom":subQ0})])],"isStart":false});}
            var Q27;
            {var subQ0=sQuery(id+"F0.wireOp",EDGE,"E3");Q27=makeQuery(id+"F2.opExtrude","CAP_EDGE",EDGE,{"disambiguationData":[OSD([subQ0]),TDD([makeQuery(id+"F0.imprint","IMPRINT",EDGE,{"disambiguationData":[TD([[makeQuery(id+"F0.imprint","INTERSECT",VERTEX,{"derivedFrom":[subQ0,sQuery(id+"F0.wireOp",EDGE,"E30")]}),1.0]])],"derivedFrom":subQ0})])],"isStart":false});}
            var Q28;
            {var subQ0=sQuery(id+"F0.wireOp",EDGE,"E3");Q28=makeQuery(id+"F2.opExtrude","CAP_EDGE",EDGE,{"disambiguationData":[OSD([subQ0]),TDD([makeQuery(id+"F0.imprint","IMPRINT",EDGE,{"disambiguationData":[TD([[makeQuery(id+"F0.imprint","INTERSECT",VERTEX,{"derivedFrom":[subQ0,sQuery(id+"F0.wireOp",EDGE,"E32")]}),1.0]])],"derivedFrom":subQ0})])],"isStart":false});}
            var Q29;
            {var subQ0=sQuery(id+"F0.wireOp",EDGE,"E49.MirrorCS");Q29=makeQuery(id+"F2.opExtrude","CAP_EDGE",EDGE,{"disambiguationData":[OSD([subQ0]),TDD([makeQuery(id+"F0.imprint","IMPRINT",EDGE,{"disambiguationData":[TD([[makeQuery(id+"F0.imprint","INTERSECT",VERTEX,{"derivedFrom":[subQ0,sQuery(id+"F0.wireOp",EDGE,"E78.MirrorCS")]}),1.0]])],"derivedFrom":subQ0})])],"isStart":false});}
            var Q30;
            {var subQ0=sQuery(id+"F0.wireOp",EDGE,"E49.MirrorCS");Q30=makeQuery(id+"F2.opExtrude","CAP_EDGE",EDGE,{"disambiguationData":[OSD([subQ0]),TDD([makeQuery(id+"F0.imprint","IMPRINT",EDGE,{"disambiguationData":[TD([[makeQuery(id+"F0.imprint","INTERSECT",VERTEX,{"derivedFrom":[subQ0,sQuery(id+"F0.wireOp",EDGE,"E80.MirrorCS")]}),1.0]])],"derivedFrom":subQ0})])],"isStart":false});}
            var Q31;
            {var subQ0=sQuery(id+"F0.wireOp",EDGE,"E3");Q31=makeQuery(id+"F2.opExtrude","CAP_EDGE",EDGE,{"disambiguationData":[OSD([subQ0]),TDD([makeQuery(id+"F0.imprint","IMPRINT",EDGE,{"disambiguationData":[TD([[makeQuery(id+"F0.imprint","INTERSECT",VERTEX,{"derivedFrom":[subQ0,sQuery(id+"F0.wireOp",EDGE,"E34")]}),1.0]])],"derivedFrom":subQ0})])],"isStart":false});}
            var Q32;
            {var subQ0=sQuery(id+"F0.wireOp",EDGE,"E3");Q32=makeQuery(id+"F2.opExtrude","CAP_EDGE",EDGE,{"disambiguationData":[OSD([subQ0]),TDD([makeQuery(id+"F0.imprint","IMPRINT",EDGE,{"disambiguationData":[TD([[makeQuery(id+"F0.imprint","INTERSECT",VERTEX,{"derivedFrom":[subQ0,sQuery(id+"F0.wireOp",EDGE,"E36")]}),1.0]])],"derivedFrom":subQ0})])],"isStart":false});}
            var Q33;
            {var subQ0=sQuery(id+"F0.wireOp",EDGE,"E49.MirrorCS");Q33=makeQuery(id+"F2.opExtrude","CAP_EDGE",EDGE,{"disambiguationData":[OSD([subQ0]),TDD([makeQuery(id+"F0.imprint","IMPRINT",EDGE,{"disambiguationData":[TD([[makeQuery(id+"F0.imprint","INTERSECT",VERTEX,{"derivedFrom":[subQ0,sQuery(id+"F0.wireOp",EDGE,"E82.MirrorCS")]}),1.0]])],"derivedFrom":subQ0})])],"isStart":false});}
            var Q34;
            {var subQ0=sQuery(id+"F0.wireOp",EDGE,"E49.MirrorCS");Q34=makeQuery(id+"F2.opExtrude","CAP_EDGE",EDGE,{"disambiguationData":[OSD([subQ0]),TDD([makeQuery(id+"F0.imprint","IMPRINT",EDGE,{"disambiguationData":[TD([[makeQuery(id+"F0.imprint","INTERSECT",VERTEX,{"derivedFrom":[subQ0,sQuery(id+"F0.wireOp",EDGE,"E84.MirrorCS")]}),1.0]])],"derivedFrom":subQ0})])],"isStart":false});}
            var Q35;
            {var subQ0=sQuery(id+"F0.wireOp",EDGE,"E3");Q35=makeQuery(id+"F2.opExtrude","CAP_EDGE",EDGE,{"disambiguationData":[OSD([subQ0]),TDD([makeQuery(id+"F0.imprint","IMPRINT",EDGE,{"disambiguationData":[TD([[makeQuery(id+"F0.imprint","INTERSECT",VERTEX,{"derivedFrom":[subQ0,sQuery(id+"F0.wireOp",EDGE,"E38")]}),1.0]])],"derivedFrom":subQ0})])],"isStart":false});}
            var Q36;
            {var subQ0=sQuery(id+"F0.wireOp",EDGE,"E3");Q36=makeQuery(id+"F2.opExtrude","CAP_EDGE",EDGE,{"disambiguationData":[OSD([subQ0]),TDD([makeQuery(id+"F0.imprint","IMPRINT",EDGE,{"disambiguationData":[TD([[makeQuery(id+"F0.imprint","INTERSECT",VERTEX,{"derivedFrom":[subQ0,sQuery(id+"F0.wireOp",EDGE,"E40")]}),1.0]])],"derivedFrom":subQ0})])],"isStart":false});}
            var Q37;
            {var subQ0=sQuery(id+"F0.wireOp",EDGE,"E49.MirrorCS");Q37=makeQuery(id+"F2.opExtrude","CAP_EDGE",EDGE,{"disambiguationData":[OSD([subQ0]),TDD([makeQuery(id+"F0.imprint","IMPRINT",EDGE,{"disambiguationData":[TD([[makeQuery(id+"F0.imprint","INTERSECT",VERTEX,{"derivedFrom":[subQ0,sQuery(id+"F0.wireOp",EDGE,"E86.MirrorCS")]}),1.0]])],"derivedFrom":subQ0})])],"isStart":false});}
            var Q38;
            {var subQ0=sQuery(id+"F0.wireOp",EDGE,"E49.MirrorCS");Q38=makeQuery(id+"F2.opExtrude","CAP_EDGE",EDGE,{"disambiguationData":[OSD([subQ0]),TDD([makeQuery(id+"F0.imprint","IMPRINT",EDGE,{"disambiguationData":[TD([[makeQuery(id+"F0.imprint","INTERSECT",VERTEX,{"derivedFrom":[subQ0,sQuery(id+"F0.wireOp",EDGE,"E88.MirrorCS")]}),1.0]])],"derivedFrom":subQ0})])],"isStart":false});}
            var Q39;
            {var subQ0=sQuery(id+"F0.wireOp",EDGE,"E49.MirrorCS");Q39=makeQuery(id+"F2.opExtrude","CAP_EDGE",EDGE,{"disambiguationData":[OSD([subQ0]),TDD([makeQuery(id+"F0.imprint","IMPRINT",EDGE,{"disambiguationData":[TD([[makeQuery(id+"F0.imprint","INTERSECT",VERTEX,{"derivedFrom":[subQ0,sQuery(id+"F0.wireOp",EDGE,"E90.MirrorCS")]}),1.0]])],"derivedFrom":subQ0})])],"isStart":false});}
            var Q40;
            {var subQ0=sQuery(id+"F0.wireOp",EDGE,"E49.MirrorCS");Q40=makeQuery(id+"F2.opExtrude","CAP_EDGE",EDGE,{"disambiguationData":[OSD([subQ0]),TDD([makeQuery(id+"F0.imprint","IMPRINT",EDGE,{"disambiguationData":[TD([[makeQuery(id+"F0.imprint","INTERSECT",VERTEX,{"derivedFrom":[subQ0,sQuery(id+"F0.wireOp",EDGE,"E93.MirrorCS")]}),1.0]])],"derivedFrom":subQ0})])],"isStart":false});}
            var Q41;
            {var subQ0=sQuery(id+"F0.wireOp",EDGE,"E3");Q41=makeQuery(id+"F2.opExtrude","CAP_EDGE",EDGE,{"disambiguationData":[OSD([subQ0]),TDD([makeQuery(id+"F0.imprint","IMPRINT",EDGE,{"disambiguationData":[TD([[makeQuery(id+"F0.imprint","INTERSECT",VERTEX,{"derivedFrom":[subQ0,sQuery(id+"F0.wireOp",EDGE,"E42")]}),1.0]])],"derivedFrom":subQ0})])],"isStart":false});}
            var Q42;
            {var subQ0=sQuery(id+"F0.wireOp",EDGE,"E3");Q42=makeQuery(id+"F2.opExtrude","CAP_EDGE",EDGE,{"disambiguationData":[OSD([subQ0]),TDD([makeQuery(id+"F0.imprint","IMPRINT",EDGE,{"disambiguationData":[TD([[makeQuery(id+"F0.imprint","INTERSECT",VERTEX,{"derivedFrom":[subQ0,sQuery(id+"F0.wireOp",EDGE,"E46")]}),1.0]])],"derivedFrom":subQ0})])],"isStart":false});}
            var Q43;
            {var subQ0=sQuery(id+"F0.wireOp",EDGE,"E3");Q43=makeQuery(id+"F2.opExtrude","CAP_EDGE",EDGE,{"disambiguationData":[OSD([subQ0]),TDD([makeQuery(id+"F0.imprint","IMPRINT",EDGE,{"disambiguationData":[TD([[makeQuery(id+"F0.imprint","INTERSECT",VERTEX,{"derivedFrom":[subQ0,sQuery(id+"F0.wireOp",EDGE,"E44")]}),1.0]])],"derivedFrom":subQ0})])],"isStart":false});}
            fillet(context, id + "F5", {"entities" : qUnion([Q0, Q1, Q2, Q3, Q4, Q5, Q6, Q7, Q8, Q9, Q10, Q11, Q12, Q13, Q14, Q15, Q16, Q17, Q18, Q19, Q20, Q21, Q22, Q23, Q24, Q25, Q26, Q27, Q28, Q29, Q30, Q31, Q32, Q33, Q34, Q35, Q36, Q37, Q38, Q39, Q40, Q41, Q42, Q43]), "radius" : 1 * mm, "tangentPropagation" : true, "allowEdgeOverflow" : false});
        }
    });
